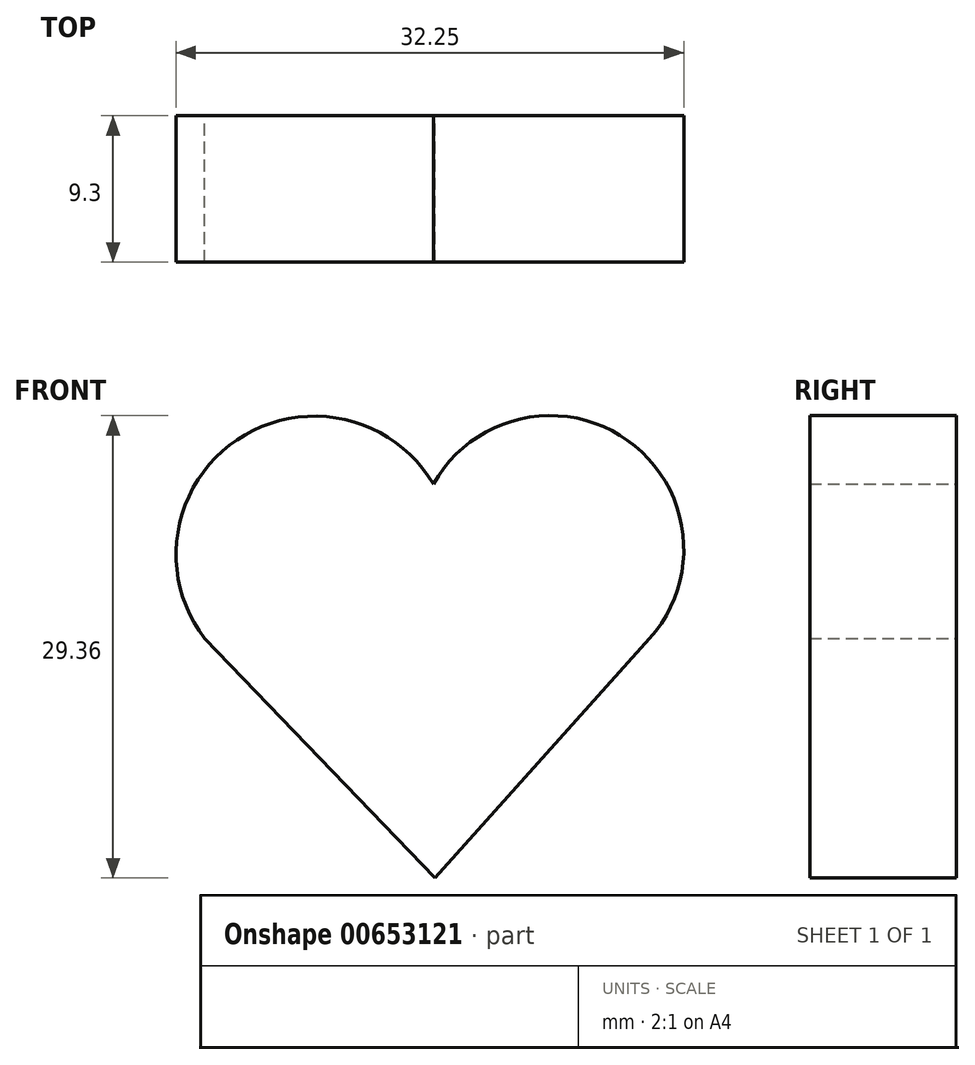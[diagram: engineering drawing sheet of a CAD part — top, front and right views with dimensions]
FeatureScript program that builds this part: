
annotation { "Feature Type Name" : "Feature", "Feature Type Description" : "" }
export const myFeature = defineFeature(function(context is Context, id is Id, definition is map)
    precondition{}
    {
        {
            var Q0;
            Q0=qCreatedBy(makeId("Front.planeOp"),FACE);
            var sketch = newSketch(context, id + "F0", { "sketchPlane" : qUnion([Q0])});
            skLineSegment(sketch, "E0", {"start": v(4.98, -0.72) * mm, "end": v(-9.66, 14.49) * mm});
            skLineSegment(sketch, "E1", {"start": v(4.98, -0.72) * mm, "end": v(18.6, 14.49) * mm});
            skArc(sketch, "E2", {"start": v(4.86, 24.28) * mm, "mid": v(-7.6, 27.1) * mm, "end": v(-9.66, 14.49) * mm});
            skArc(sketch, "E3", {"start": v(18.6, 14.49) * mm, "mid": v(17.2, 27.06) * mm, "end": v(4.86, 24.28) * mm});
            skSolve(sketch);
        }
        {
            var Q0;
            Q0=sQuery(id+"F0.wireOp",EDGE,"E2");
            var Q1;
            Q1=sQuery(id+"F0.wireOp",EDGE,"E3");
            var Q2;
            Q2=sQuery(id+"F0.wireOp",EDGE,"E1");
            var Q3;
            Q3=sQuery(id+"F0.wireOp",EDGE,"E0");
            extrude(context, id + "F1", {"bodyType" : ToolBodyType.SURFACE, "surfaceEntities" : qUnion([Q0, Q1, Q2, Q3]), "oppositeDirection" : true, "depth" : 9.3 * mm, "offsetDistance" : 25 * mm});
        }
    });
